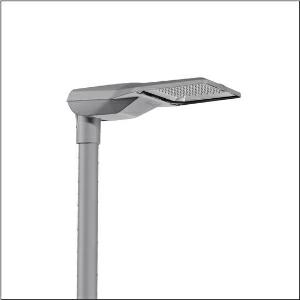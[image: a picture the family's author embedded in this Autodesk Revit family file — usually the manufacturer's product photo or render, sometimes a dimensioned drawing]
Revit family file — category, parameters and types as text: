
# Revit family: streetlight_sl_21_midi___st1_5a_5xe7p43a08lb_c2d0
name_source: partatom
category: Lighting Fixtures
units: mm (PartAtom-declared; Revit-internal decimal feet)

## family parameters
Cut with Voids When Loaded = No
Host = Face
Light Source = No
Part Type = Normal
Room Calculation Point = No
Round Connector Dimension = Use Diameter
Shared = No

## types (1)
- --- (1 x LED, 14690 lm, 98.3 W, 4000K)
    Apparent Load = 98 VA
    CIE Flux Codes = 22 53 95 100 100
    Color Rendering = 70
    Color Temperature = 4000K
    Default Elevation = 1800 mm
    Description = Streetlight SL 21 midi, mast luminaire, primary light control with lens, of PMMA, primary optical cover: cover, of toughened safety glass, transparent, light distribution: ST1.5a, light emission: direct distribution, primary light characteristic: asymmetric, installation type: post-top, side-entry, LED, 3G 1.5mm², High Power LED, rated luminous flux: 14.690lm, luminous efficacy: 149lm/W, light colour: 740, colour temperature: 4000K, control: overheat protection, constant luminous flux control, time-dependent luminous flux control, flexible luminous flux parameterisation, mains connection: 220..240V, AC, 50/60Hz, connection cable pre-assembled, cable length: 10,5m, wiring characteristics: H07RN-F, start of lifetime: 98W, end of service life: 101W, reduction: 45W, luminaire housing, of diecast aluminium, powder-coated, Siteco® metallic grey (DB 702S), corrosivity category C5 mid according to DIN EN ISO 12944, please order mast flange separately, inclination adjustable: 0°, 5°, 10°, 15°, sealing non-destructively replaceable, multi-level sealing system, length: 644mm, width: 335mm, height: 110mm, mast flange for spigot size: 42mm (side-entry): 5XC10008XM4, 60/48mm (side-entry/post-top): 5XC10108XM2, 76/60mm (side-entry/post-top): 5XC10108XM1, protection rating (complete): IP66, insulation class (complete): insulation class II (safety insulation), certification: CE, ENEC, ENEC+, VDE, impact resistance: IK09, permissible operating ambient temperature for outdoor applications: -40..+50°C, standard-compliant lighting for roads and squares, packaging unit: 1 piece

Light Distribution: ST1.5a
    Height = 111 mm
    Lamp = 1 x LED
    Lamp Light Flux = 14690 lm
    Lamp Power = 98.3 W
    Lamp count = 1
    Length = 644 mm
    Luminous efficacy = 149 lm/W
    Manufacturer = Siteco
    ModVariant = No
    Model = 5XE7P43A08LB
    Number of Poles = 1
    OnlyDefault = Yes
    Power Factor = 1
    Product Name = Streetlight SL 21 midi | ST1.5a
    Product group = mast luminaire | pylon top
    ProductGroupID = 6100
    Protection Class = Protection class II
    Protection Degree = IP 66
    RLX_Detail_Level = 1
    RLX_Emergency_Light_Flux = 0 lm
    RLX_Emergency_Type = 0
    RLX_Emergency_Type_DB = No
    RlxData = <blob elided: 94041 chars, md5=852a38b0>
    Socket = socket
    Standby Power = 0 W
    System Light Flux = 14690 lm
    System Power = 98 W
    Type Comments = factory setting: luminous flux: 100 % | Output Level: 100 % | 1020 mA
    Type Image = l_1004298.jpg
    URL = http://relux.com
    VarID = @adj_126991
    Voltage = 0 V
    Weight = 0.00 kg
    Width = 336 mm

## geometry (parser evidence)
native form markers: Blend x4, Sweep x12
no freeform markers — native parametric forms only
